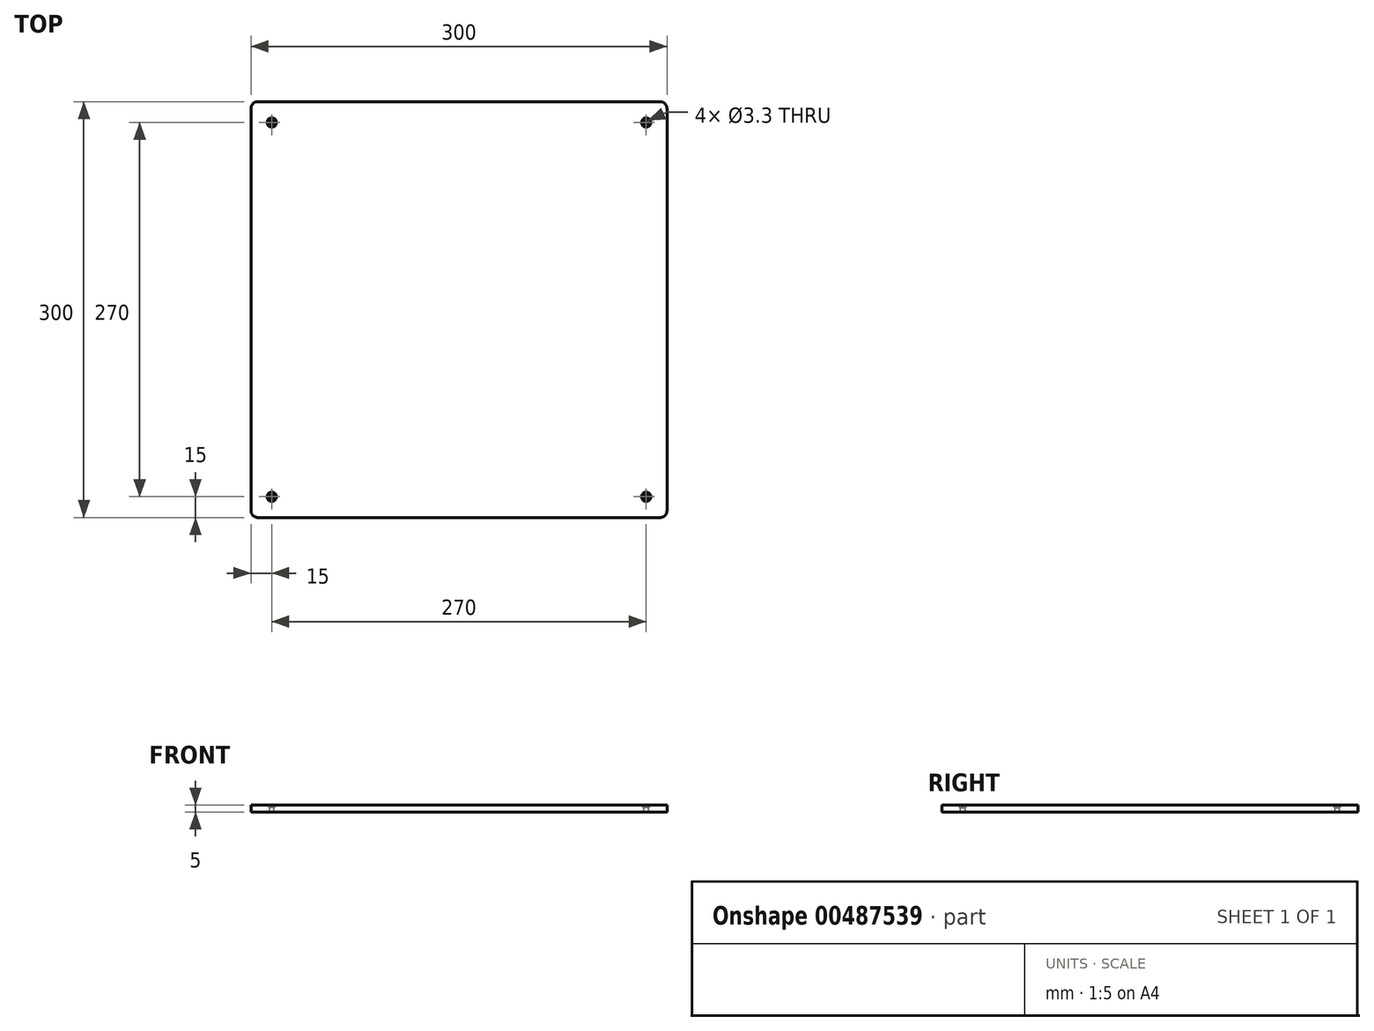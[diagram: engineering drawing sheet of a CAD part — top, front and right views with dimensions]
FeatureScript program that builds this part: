
annotation { "Feature Type Name" : "Feature", "Feature Type Description" : "" }
export const myFeature = defineFeature(function(context is Context, id is Id, definition is map)
    precondition{}
    {
        {
            var Q0;
            Q0=qCreatedBy(makeId("Top.planeOp"),FACE);
            var sketch = newSketch(context, id + "F0", { "sketchPlane" : qUnion([Q0])});
            skLineSegment(sketch, "E0.bottom", {"start": v(150, -150) * mm, "end": v(-150, -150) * mm});
            skLineSegment(sketch, "E0.top", {"start": v(150, 150) * mm, "end": v(-150, 150) * mm});
            skLineSegment(sketch, "E0.left", {"start": v(150, -150) * mm, "end": v(150, 150) * mm});
            skLineSegment(sketch, "E0.right", {"start": v(-150, -150) * mm, "end": v(-150, 150) * mm});
            skPoint(sketch, "E0.middle", {"position": v(0, 0) * mm});
            skPoint(sketch, "E1", {"position": v(-135, -135) * mm});
            skPoint(sketch, "E2.MirrorP", {"position": v(-135, 135) * mm});
            skPoint(sketch, "E3.MirrorP", {"position": v(135, 135) * mm});
            skPoint(sketch, "E4.MirrorP", {"position": v(135, -135) * mm});
            skSolve(sketch);
        }
        {
            var Q0;
            Q0 = qSketchRegion(id + "F0", true);
            extrude(context, id + "F1", {"entities" : qUnion([Q0]), "oppositeDirection" : true, "depth" : 5 * mm, "offsetDistance" : 25 * mm});
        }
        {
            var Q0;
            Q0=sQuery(id+"F0.wireOp",VERTEX,"E2.MirrorP");
            var Q1;
            Q1=sQuery(id+"F0.wireOp",VERTEX,"E1");
            var Q2;
            Q2=sQuery(id+"F0.wireOp",VERTEX,"E4.MirrorP");
            var Q3;
            Q3=sQuery(id+"F0.wireOp",VERTEX,"E3.MirrorP");
            var Q4;
            Q4=makeQuery(id+"F1.opExtrude","SWEPT_BODY",BODY,{"disambiguationData":[OSD([sQuery(id+"F0.wireOp",EDGE,"E0.bottom"),sQuery(id+"F0.wireOp",EDGE,"E0.top"),sQuery(id+"F0.wireOp",EDGE,"E0.left"),sQuery(id+"F0.wireOp",EDGE,"E0.right")])]});
            hole(context, id + "F2", {"style" : HoleStyle.C_SINK, "endStyle" : HoleEndStyle.THROUGH, "standardTappedOrClearance" : lookupTablePath({ "standard" : "ISO", "fit" : "Normal", "size" : "M3", "type" : "Clearance" }), "standardBlindInLast" : lookupTablePath({ "fit" : "Standard", "standard" : "ISO", "size" : "M3", "type" : "Clearance" }), "holeDiameter" : 3.3 * mm, "cSinkDiameter" : 6.72 * mm, "cSinkAngle" : 90 * degree, "isTappedThrough" : true, "tappedDepth" : 12 * mm, "tapClearance" : 3, "locations" : qUnion([Q0, Q1, Q2, Q3]), "scope" : qUnion([Q4])});
        }
        {
            var Q0;
            Q0=makeQuery(id+"F1.opExtrude","SWEPT_EDGE",EDGE,{"disambiguationData":[OSD([sQuery(id+"F0.wireOp",EDGE,"E0.top"),sQuery(id+"F0.wireOp",EDGE,"E0.right")])]});
            var Q1;
            Q1=makeQuery(id+"F1.opExtrude","SWEPT_EDGE",EDGE,{"disambiguationData":[OSD([sQuery(id+"F0.wireOp",EDGE,"E0.top"),sQuery(id+"F0.wireOp",EDGE,"E0.left")])]});
            var Q2;
            Q2=makeQuery(id+"F1.opExtrude","SWEPT_EDGE",EDGE,{"disambiguationData":[OSD([sQuery(id+"F0.wireOp",EDGE,"E0.bottom"),sQuery(id+"F0.wireOp",EDGE,"E0.left")])]});
            var Q3;
            Q3=makeQuery(id+"F1.opExtrude","SWEPT_EDGE",EDGE,{"disambiguationData":[OSD([sQuery(id+"F0.wireOp",EDGE,"E0.bottom"),sQuery(id+"F0.wireOp",EDGE,"E0.right")])]});
            fillet(context, id + "F3", {"entities" : qUnion([Q0, Q1, Q2, Q3]), "radius" : 5 * mm, "tangentPropagation" : true, "allowEdgeOverflow" : false});
        }
    });
